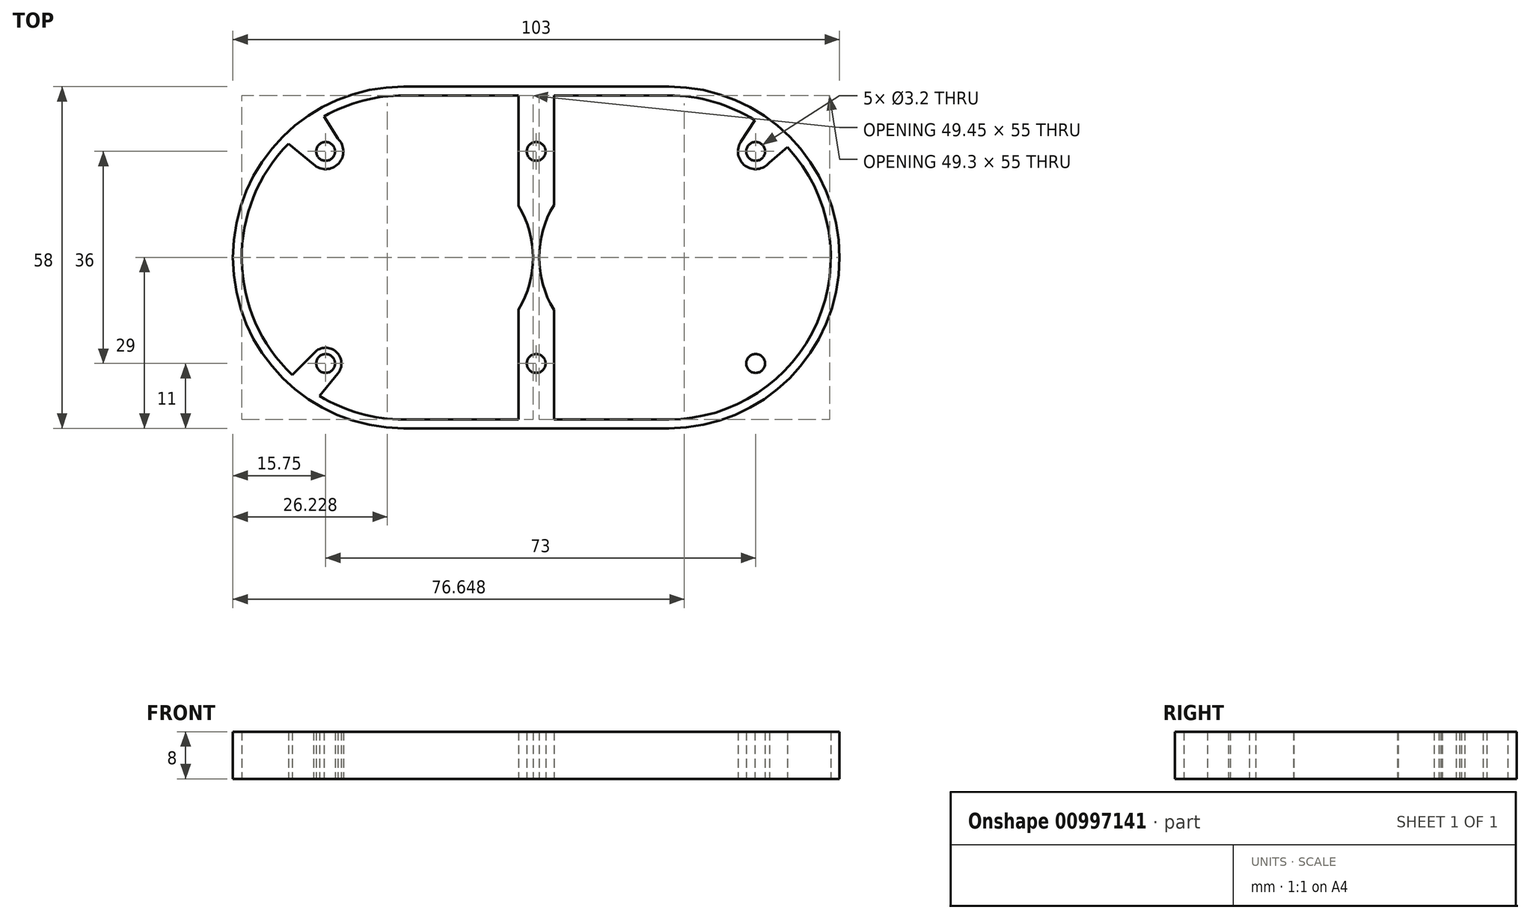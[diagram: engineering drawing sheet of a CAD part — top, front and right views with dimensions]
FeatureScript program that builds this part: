
annotation { "Feature Type Name" : "Feature", "Feature Type Description" : "" }
export const myFeature = defineFeature(function(context is Context, id is Id, definition is map)
    precondition{}
    {
        {
            var Q0;
            Q0=qCreatedBy(makeId("Top.planeOp"),FACE);
            var sketch = newSketch(context, id + "F0", { "sketchPlane" : qUnion([Q0])});
            skCircle(sketch, "E0", {"center": v(-6.8, -0.03) * mm, "radius": 17 * mm});
            skLineSegment(sketch, "E1.0", {"start": v(-41.75, 0) * mm, "end": v(-41.75, 0) * mm});
            skLineSegment(sketch, "E1.1", {"start": v(-41.75, 0) * mm, "end": v(-41.75, 0) * mm});
            skLineSegment(sketch, "E1.2", {"start": v(-41.75, 0) * mm, "end": v(-41.75, 0) * mm});
            skLineSegment(sketch, "E1.4", {"start": v(-41.75, 0) * mm, "end": v(-41.75, 0) * mm});
            skLineSegment(sketch, "E1.6", {"start": v(-41.75, 0) * mm, "end": v(-41.75, 0) * mm});
            skCircle(sketch, "E2", {"center": v(28.25, 0) * mm, "radius": 17 * mm});
            skCircle(sketch, "E3", {"center": v(48, 18) * mm, "radius": 1.6 * mm});
            skCircle(sketch, "E4", {"center": v(48, -18) * mm, "radius": 1.6 * mm});
            skLineSegment(sketch, "E5", {"start": v(48, -18) * mm, "end": v(48, 20.03) * mm});
            skCircle(sketch, "E6", {"center": v(-25, -18) * mm, "radius": 1.6 * mm});
            skCircle(sketch, "E7", {"center": v(-25, 18) * mm, "radius": 1.6 * mm});
            skPoint(sketch, "E8.0.midPoint", {"position": v(-52.43, -18) * mm});
            skLineSegment(sketch, "E9.top", {"start": v(10.75, -30.5) * mm, "end": v(10.75, -30.5) * mm});
            skLineSegment(sketch, "E10", {"start": v(10.75, 30.5) * mm, "end": v(10.75, -30.5) * mm, "construction": true});
            skCircle(sketch, "E11", {"center": v(10.75, 18) * mm, "radius": 1.6 * mm});
            skCircle(sketch, "E12", {"center": v(10.75, -18) * mm, "radius": 1.6 * mm});
            skLineSegment(sketch, "E13.bottom", {"start": v(-11.75, -29) * mm, "end": v(33.25, -29) * mm});
            skLineSegment(sketch, "E13.top", {"start": v(-11.75, 29) * mm, "end": v(33.25, 29) * mm});
            skLineSegment(sketch, "E13.left", {"start": v(-11.75, -29) * mm, "end": v(-11.75, 29) * mm});
            skLineSegment(sketch, "E13.right", {"start": v(33.25, -29) * mm, "end": v(33.25, 29) * mm});
            skPoint(sketch, "E13.middle", {"position": v(10.75, 0) * mm});
            skPoint(sketch, "E13.middle.positionSnap0", {"position": v(10.75, 0) * mm});
            skPoint(sketch, "E13.centerSnap0", {"position": v(10.75, 0) * mm});
            skArc(sketch, "E14", {"start": v(-11.75, 29) * mm, "mid": v(-40.75, 0) * mm, "end": v(-11.75, -29) * mm});
            skArc(sketch, "E15", {"start": v(33.25, 29) * mm, "mid": v(62.25, 0) * mm, "end": v(33.25, -29) * mm});
            skLineSegment(sketch, "E16.bottom", {"start": v(33.25, 27.5) * mm, "end": v(-11.75, 27.5) * mm});
            skLineSegment(sketch, "E16.top", {"start": v(33.25, -27.5) * mm, "end": v(-11.75, -27.5) * mm});
            skLineSegment(sketch, "E16.left", {"start": v(33.25, 27.5) * mm, "end": v(33.25, -27.5) * mm});
            skLineSegment(sketch, "E16.right", {"start": v(-11.75, 27.5) * mm, "end": v(-11.75, -27.5) * mm});
            skArc(sketch, "E17", {"start": v(-11.75, 27.5) * mm, "mid": v(-39.25, 0) * mm, "end": v(-11.75, -27.5) * mm});
            skArc(sketch, "E18", {"start": v(33.25, 27.5) * mm, "mid": v(60.75, 0) * mm, "end": v(33.25, -27.5) * mm});
            skCircle(sketch, "E19", {"center": v(-25, 18) * mm, "radius": 3 * mm});
            skLineSegment(sketch, "E20", {"start": v(-6.8, -0.03) * mm, "end": v(-28.77, 21.6) * mm});
            skLineSegment(sketch, "E21", {"start": v(-6.8, -0.03) * mm, "end": v(-28.8, -21.57) * mm});
            skLineSegment(sketch, "E22", {"start": v(-27.06, 15.82) * mm, "end": v(-31.32, 19.32) * mm});
            skLineSegment(sketch, "E23", {"start": v(-22.93, 20.17) * mm, "end": v(-25.3, 23.93) * mm});
            skCircle(sketch, "E24", {"center": v(-25, -18) * mm, "radius": 2.67 * mm});
            skCircle(sketch, "E25", {"center": v(10.75, -18) * mm, "radius": 3 * mm});
            skCircle(sketch, "E26", {"center": v(48, -18) * mm, "radius": 3 * mm});
            skCircle(sketch, "E27", {"center": v(48, 18) * mm, "radius": 3 * mm});
            skCircle(sketch, "E28", {"center": v(10.75, 18) * mm, "radius": 3 * mm});
            skLineSegment(sketch, "E29", {"start": v(7.75, 27.5) * mm, "end": v(7.75, -27.5) * mm});
            skLineSegment(sketch, "E30", {"start": v(13.75, 27.5) * mm, "end": v(13.75, -27.5) * mm});
            skLineSegment(sketch, "E31", {"start": v(45.5, 19.64) * mm, "end": v(47.88, 23.29) * mm});
            skLineSegment(sketch, "E32", {"start": v(50.32, 16.1) * mm, "end": v(53.4, 18.7) * mm});
            skLineSegment(sketch, "E33", {"start": v(49.63, -15.48) * mm, "end": v(53.51, -18.6) * mm});
            skLineSegment(sketch, "E34", {"start": v(45.59, -19.79) * mm, "end": v(48.54, -22.86) * mm});
            skLineSegment(sketch, "E35", {"start": v(-22.92, -19.68) * mm, "end": v(-26.01, -23.51) * mm});
            skLineSegment(sketch, "E36", {"start": v(-26.89, -16.11) * mm, "end": v(-30.7, -19.93) * mm});
            skSolve(sketch);
        }
        {
            var Q0;
            {var subQ0=sQuery(id+"F0.wireOp",EDGE,"E15");Q0=makeQuery(id+"F0.imprint","IMPRINT",FACE,{"disambiguationData":[TD([[makeQuery(id+"F0.imprint","IMPRINT",EDGE,{"derivedFrom":subQ0}),-1.0]])]});}
            var Q1;
            {var subQ1=sQuery(id+"F0.wireOp",EDGE,"E13.top");Q1=makeQuery(id+"F0.imprint","IMPRINT",FACE,{"disambiguationData":[TD([[makeQuery(id+"F0.imprint","IMPRINT",EDGE,{"derivedFrom":subQ1}),-1.0]])]});}
            var Q2;
            {var subQ4=sQuery(id+"F0.wireOp",EDGE,"E13.bottom");Q2=makeQuery(id+"F0.imprint","IMPRINT",FACE,{"disambiguationData":[TD([[makeQuery(id+"F0.imprint","IMPRINT",EDGE,{"derivedFrom":subQ4}),1.0]])]});}
            var Q3;
            {var subQ0=sQuery(id+"F0.wireOp",EDGE,"E14");Q3=makeQuery(id+"F0.imprint","IMPRINT",FACE,{"disambiguationData":[TD([[makeQuery(id+"F0.imprint","IMPRINT",EDGE,{"derivedFrom":subQ0}),1.0]])]});}
            var Q4;
            {var subQ0=sQuery(id+"F0.wireOp",EDGE,"E29");var subQ1=sQuery(id+"F0.wireOp",EDGE,"E16.top");var subQ2=makeQuery(id+"F0.imprint","INTERSECT",VERTEX,{"derivedFrom":[subQ1,subQ0]});Q4=makeQuery(id+"F0.imprint","IMPRINT",FACE,{"disambiguationData":[TD([[makeQuery(id+"F0.imprint","IMPRINT",EDGE,{"disambiguationData":[TD([[subQ2,1.0]])],"derivedFrom":subQ1}),-1.0]])]});}
            var Q5;
            Q5=makeQuery(id+"F0.imprint","IMPRINT",FACE,{"disambiguationData":[TD([[makeQuery(id+"F0.imprint","IMPRINT",EDGE,{"derivedFrom":sQuery(id+"F0.wireOp",EDGE,"E12")}),-1.0]])]});
            var Q6;
            {var subQ6=sQuery(id+"F0.wireOp",EDGE,"E29");var subQ11=sQuery(id+"F0.wireOp",EDGE,"E0");var subQ12=makeQuery(id+"F0.imprint","INTERSECT",VERTEX,{"disambiguationData":[OD(0.0)],"derivedFrom":[subQ11,subQ6]});Q6=makeQuery(id+"F0.imprint","IMPRINT",FACE,{"disambiguationData":[TD([[makeQuery(id+"F0.imprint","IMPRINT",EDGE,{"disambiguationData":[TD([[subQ12,1.0]])],"derivedFrom":subQ11}),-1.0]])]});}
            var Q7;
            {var subQ0=sQuery(id+"F0.wireOp",EDGE,"E29");var subQ1=sQuery(id+"F0.wireOp",EDGE,"E16.bottom");var subQ2=makeQuery(id+"F0.imprint","INTERSECT",VERTEX,{"derivedFrom":[subQ1,subQ0]});Q7=makeQuery(id+"F0.imprint","IMPRINT",FACE,{"disambiguationData":[TD([[makeQuery(id+"F0.imprint","IMPRINT",EDGE,{"disambiguationData":[TD([[subQ2,1.0]])],"derivedFrom":subQ1}),1.0]])]});}
            var Q8;
            Q8=makeQuery(id+"F0.imprint","IMPRINT",FACE,{"disambiguationData":[TD([[makeQuery(id+"F0.imprint","IMPRINT",EDGE,{"derivedFrom":sQuery(id+"F0.wireOp",EDGE,"E11")}),-1.0]])]});
            var Q9;
            {var subQ3=sQuery(id+"F0.wireOp",EDGE,"E35");Q9=makeQuery(id+"F0.imprint","IMPRINT",FACE,{"disambiguationData":[TD([[makeQuery(id+"F0.imprint","IMPRINT",EDGE,{"derivedFrom":subQ3}),-1.0]])]});}
            var Q10;
            {var subQ3=sQuery(id+"F0.wireOp",EDGE,"E36");Q10=makeQuery(id+"F0.imprint","IMPRINT",FACE,{"disambiguationData":[TD([[makeQuery(id+"F0.imprint","IMPRINT",EDGE,{"derivedFrom":subQ3}),1.0]])]});}
            var Q11;
            {var subQ0=sQuery(id+"F0.wireOp",EDGE,"E21");var subQ1=sQuery(id+"F0.wireOp",EDGE,"E6");var subQ5=makeQuery(id+"F0.imprint","INTERSECT",VERTEX,{"disambiguationData":[OD(0.0)],"derivedFrom":[subQ1,subQ0]});Q11=makeQuery(id+"F0.imprint","IMPRINT",FACE,{"disambiguationData":[TD([[makeQuery(id+"F0.imprint","IMPRINT",EDGE,{"disambiguationData":[TD([[subQ5,-1.0]])],"derivedFrom":subQ1}),-1.0]])]});}
            var Q12;
            {var subQ2=sQuery(id+"F0.wireOp",EDGE,"E21");var subQ4=sQuery(id+"F0.wireOp",EDGE,"E6");var subQ5=makeQuery(id+"F0.imprint","INTERSECT",VERTEX,{"disambiguationData":[OD(0.0)],"derivedFrom":[subQ4,subQ2]});Q12=makeQuery(id+"F0.imprint","IMPRINT",FACE,{"disambiguationData":[TD([[makeQuery(id+"F0.imprint","IMPRINT",EDGE,{"disambiguationData":[TD([[subQ5,1.0]])],"derivedFrom":subQ4}),-1.0]])]});}
            var Q13;
            {var subQ0=sQuery(id+"F0.wireOp",EDGE,"E33");var subQ1=sQuery(id+"F0.wireOp",EDGE,"E18");var subQ2=makeQuery(id+"F0.imprint","INTERSECT",VERTEX,{"derivedFrom":[subQ1,subQ0]});Q13=makeQuery(id+"F0.imprint","IMPRINT",FACE,{"disambiguationData":[TD([[makeQuery(id+"F0.imprint","IMPRINT",EDGE,{"disambiguationData":[TD([[subQ2,-1.0]])],"derivedFrom":subQ1}),-1.0]])]});}
            var Q14;
            Q14=makeQuery(id+"F0.imprint","IMPRINT",FACE,{"disambiguationData":[TD([[makeQuery(id+"F0.imprint","IMPRINT",EDGE,{"derivedFrom":sQuery(id+"F0.wireOp",EDGE,"E4")}),1.0]])]});
            var Q15;
            {var subQ0=sQuery(id+"F0.wireOp",EDGE,"E31");Q15=makeQuery(id+"F0.imprint","IMPRINT",FACE,{"disambiguationData":[TD([[makeQuery(id+"F0.imprint","IMPRINT",EDGE,{"derivedFrom":subQ0}),-1.0]])]});}
            var Q16;
            {var subQ2=sQuery(id+"F0.wireOp",EDGE,"E5");var subQ4=sQuery(id+"F0.wireOp",EDGE,"E3");var subQ5=makeQuery(id+"F0.imprint","INTERSECT",VERTEX,{"disambiguationData":[OD(0.0)],"derivedFrom":[subQ4,subQ2]});Q16=makeQuery(id+"F0.imprint","IMPRINT",FACE,{"disambiguationData":[TD([[makeQuery(id+"F0.imprint","IMPRINT",EDGE,{"disambiguationData":[TD([[subQ5,1.0]])],"derivedFrom":subQ4}),-1.0]])]});}
            var Q17;
            {var subQ3=sQuery(id+"F0.wireOp",EDGE,"E23");Q17=makeQuery(id+"F0.imprint","IMPRINT",FACE,{"disambiguationData":[TD([[makeQuery(id+"F0.imprint","IMPRINT",EDGE,{"derivedFrom":subQ3}),1.0]])]});}
            var Q18;
            {var subQ0=sQuery(id+"F0.wireOp",EDGE,"E20");var subQ1=sQuery(id+"F0.wireOp",EDGE,"E7");var subQ2=makeQuery(id+"F0.imprint","INTERSECT",VERTEX,{"disambiguationData":[OD(0.0)],"derivedFrom":[subQ1,subQ0]});Q18=makeQuery(id+"F0.imprint","IMPRINT",FACE,{"disambiguationData":[TD([[makeQuery(id+"F0.imprint","IMPRINT",EDGE,{"disambiguationData":[TD([[subQ2,-1.0]])],"derivedFrom":subQ1}),-1.0]])]});}
            var Q19;
            {var subQ3=sQuery(id+"F0.wireOp",EDGE,"E22");Q19=makeQuery(id+"F0.imprint","IMPRINT",FACE,{"disambiguationData":[TD([[makeQuery(id+"F0.imprint","IMPRINT",EDGE,{"derivedFrom":subQ3}),-1.0]])]});}
            var Q20;
            {var subQ2=sQuery(id+"F0.wireOp",EDGE,"E20");var subQ4=sQuery(id+"F0.wireOp",EDGE,"E7");var subQ5=makeQuery(id+"F0.imprint","INTERSECT",VERTEX,{"disambiguationData":[OD(0.0)],"derivedFrom":[subQ4,subQ2]});Q20=makeQuery(id+"F0.imprint","IMPRINT",FACE,{"disambiguationData":[TD([[makeQuery(id+"F0.imprint","IMPRINT",EDGE,{"disambiguationData":[TD([[subQ5,1.0]])],"derivedFrom":subQ4}),-1.0]])]});}
            extrude(context, id + "F1", {"entities" : qUnion([Q0, Q1, Q2, Q3, Q4, Q5, Q6, Q7, Q8, Q9, Q10, Q11, Q12, Q13, Q14, Q15, Q16, Q17, Q18, Q19, Q20]), "depth" : 8 * mm, "offsetDistance" : 25 * mm});
        }
    });
